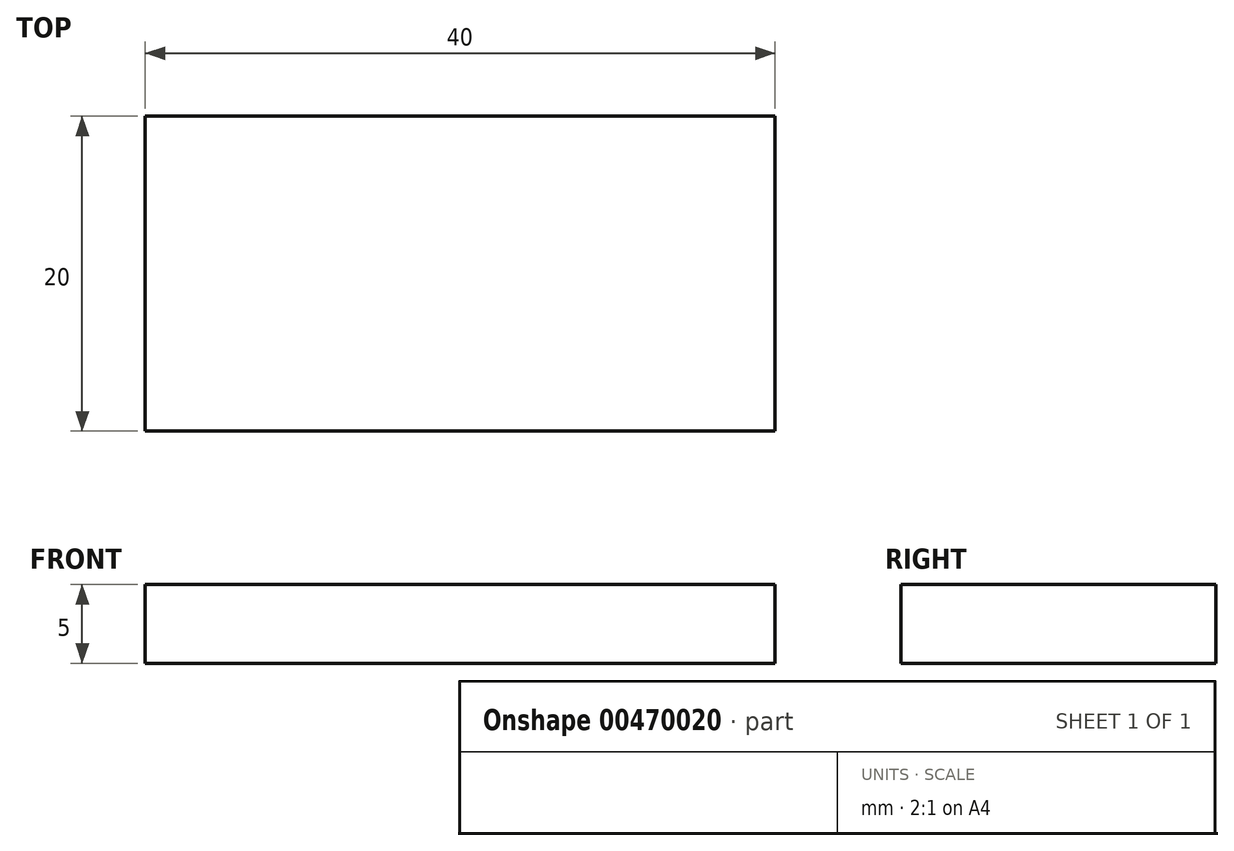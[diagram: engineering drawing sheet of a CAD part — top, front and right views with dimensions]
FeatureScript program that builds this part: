
annotation { "Feature Type Name" : "Feature", "Feature Type Description" : "" }
export const myFeature = defineFeature(function(context is Context, id is Id, definition is map)
    precondition{}
    {
        {
            var Q0;
            Q0=qCreatedBy(makeId("Top.planeOp"),FACE);
            var sketch = newSketch(context, id + "F0", { "sketchPlane" : qUnion([Q0])});
            skLineSegment(sketch, "E0.bottom", {"start": v(0, 0) * mm, "end": v(-40, 0) * mm});
            skLineSegment(sketch, "E0.top", {"start": v(0, -20) * mm, "end": v(-40, -20) * mm});
            skLineSegment(sketch, "E0.left", {"start": v(0, 0) * mm, "end": v(0, -20) * mm});
            skLineSegment(sketch, "E0.right", {"start": v(-40, 0) * mm, "end": v(-40, -20) * mm});
            skSolve(sketch);
        }
        {
            var Q0;
            Q0=makeQuery(id+"F0.imprint","IMPRINT",FACE,{"disambiguationData":[TD([[makeQuery(id+"F0.imprint","IMPRINT",EDGE,{"derivedFrom":sQuery(id+"F0.wireOp",EDGE,"E0.bottom")}),1.0]])]});
            extrude(context, id + "F1", {"entities" : qUnion([Q0]), "depth" : 5 * mm, "offsetDistance" : 25 * mm});
        }
    });
